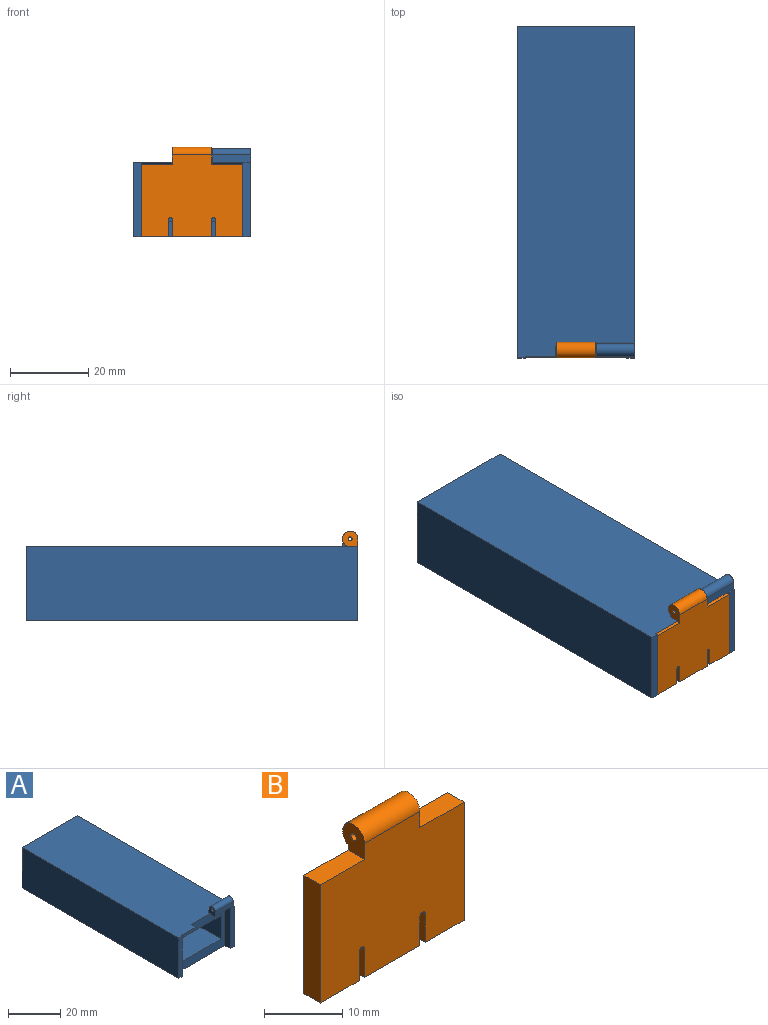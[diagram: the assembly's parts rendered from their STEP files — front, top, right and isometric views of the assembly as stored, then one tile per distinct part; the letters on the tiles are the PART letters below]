
ASSEMBLY  parts=2 mates=1
PART A: 26 faces, bbox 30x85x22.6 mm
  f0: plane 2x0.4mm, normal (0,0,1), area 0.8mm2, adj f6,f10,f12,f25
  f1: plane 19x2mm, normal (0,-1,0), area 38mm2, adj f3,f7,f9,f13
  f2: plane 7.8x1.8mm, normal (0,0,-1), area 14mm2, adj f4,f11,f13,f21
  f3: plane 85x30mm, normal (0,0,1), area 2476.5mm2, adj f1,f4,f5,f8,f9,f10,f11,f13
  f4: plane 2.6x0.5mm, normal (1,0,0), area 1.1mm2, adj f2,f3,f11,f21
  f5: plane 4.1x3.6mm, normal (-1,0,0), area 11.2mm2, adj f3,f11,f14,f20,f22,f23,f24,f25
  f6: plane 19x2mm, normal (0,-1,0), area 38mm2, adj f0,f7,f10,f12
  f7: plane 85x30mm, normal (0,0,-1), area 2472mm2, adj f1,f6,f8,f9,f10,f11,f12,f13
  f8: plane 30x19mm, normal (0,1,0), area 570mm2, adj f3,f7,f9,f10
  f9: plane 85x19mm, normal (-1,0,0), area 1615mm2, adj f1,f3,f7,f8
  f10: plane 85x22.6mm, normal (1,0,0), area 1625.1mm2, adj f0,f3,f6,f7,f8,f22,f23,f24
  f11: plane 26x19mm, normal (0,-1,0), area 244.2mm2, adj f2,f3,f4,f5,f7,f12,f13,f14
  f12: plane 19x3mm, normal (-1,0,0), area 55.9mm2, adj f0,f6,f7,f11,f14,f20
  f13: plane 19x3mm, normal (1,0,0), area 55.9mm2, adj f1,f2,f3,f7,f11,f21
  f14: plane 7.8x1.8mm, normal (0,0,-1), area 14mm2, adj f5,f11,f12,f20
  f15: plane 22x11mm, normal (0,-1,0), area 242mm2, adj f16,f17,f18,f19
  f16: plane 78x11mm, normal (1,0,0), area 858mm2, adj f11,f15,f17,f19
  f17: plane 78x22mm, normal (0,0,-1), area 1716mm2, adj f11,f15,f16,f18
  f18: plane 78x11mm, normal (-1,0,0), area 858mm2, adj f11,f15,f17,f19
  f19: plane 78x22mm, normal (0,0,1), area 1716mm2, adj f11,f15,f16,f18
  f20: cylinder r=2.69mm len=7.8mm, axis (1,0,0), area 7.4mm2, adj f5,f12,f14,f25
  f21: cylinder r=2.69mm len=7.8mm, axis (1,0,0), area 7.4mm2, adj f2,f3,f4,f13
  f22: cylinder r=1.6mm len=9.8mm, axis (-1,0,0), area 46.5mm2, adj f5,f10,f23,f25
  f23: plane 9.8x2.29mm, normal (0,0.98,0.18), area 22.8mm2, adj f3,f5,f10,f22
  f24: cylinder r=0.5mm len=9.8mm, axis (-1,0,0), area 30.8mm2, adj f5,f10
  f25: plane 9.8x2mm, normal (0,-1,0), area 19.6mm2, adj f0,f5,f10,f20,f22
PART B: 28 faces, bbox 26x11x23 mm
  f0: plane 11x10mm, normal (0,0,-1), area 110mm2, adj f4,f12,f18,f19
  f1: plane 7x3mm, normal (0,0,-1), area 21mm2, adj f2,f4,f7,f20
  f2: plane 26x19.27mm, normal (0,1,0), area 428.8mm2, adj f1,f3,f5,f6,f7,f8,f9,f10
  f3: cylinder r=2mm len=10mm, axis (-1,0,0), area 83.8mm2, adj f2,f4,f8,f10
  f4: plane 26x21mm, normal (0,-1,0), area 496.2mm2, adj f0,f1,f3,f5,f6,f7,f8,f9
  f5: plane 7x3mm, normal (0,0,-1), area 21mm2, adj f2,f4,f6,f21
  f6: plane 18.5x3mm, normal (1,0,0), area 55.5mm2, adj f2,f4,f5,f11
  f7: plane 18.5x3mm, normal (-1,0,0), area 55.5mm2, adj f1,f2,f4,f9
  f8: plane 4.5x4mm, normal (-1,0,0), area 14.2mm2, adj f2,f3,f4,f9,f27
  f9: plane 8x3mm, normal (0,0,1), area 24mm2, adj f2,f4,f7,f8
  f10: plane 4.5x4mm, normal (1,0,0), area 14.2mm2, adj f2,f3,f4,f11,f27
  f11: plane 8x3mm, normal (0,0,1), area 24mm2, adj f2,f4,f6,f10
  f12: plane 10x1.47mm, normal (0,1,0), area 14.7mm2, adj f0,f13,f18,f19
  f13: plane 10x3mm, normal (0,0.17,0.98), area 30.5mm2, adj f12,f14,f18,f19
  f14: plane 10x1mm, normal (0,1,0), area 10mm2, adj f13,f15,f18,f19
  f15: plane 10x1mm, normal (0,0,1), area 10mm2, adj f14,f16,f18,f19
  f16: plane 10x1mm, normal (0,-0.98,0.17), area 10.2mm2, adj f15,f17,f18,f19
  f17: plane 10x4.06mm, normal (0,0,1), area 40.6mm2, adj f16,f18,f19,f26
  f18: plane 11x4.5mm, normal (1,0,0), area 27.1mm2, adj f0,f4,f12,f13,f14,f15,f16,f17
  f19: plane 11x4.5mm, normal (-1,0,0), area 27.1mm2, adj f0,f4,f12,f13,f14,f15,f16,f17
  f20: plane 4.5x3mm, normal (1,0,0), area 13.5mm2, adj f1,f2,f4,f22
  f21: plane 4.5x3mm, normal (-1,0,0), area 13.5mm2, adj f2,f4,f5,f23
  f22: cylinder r=0.5mm len=3mm, axis (0,1,0), area 4.3mm2, adj f2,f4,f19,f20,f25
  f23: cylinder r=0.5mm len=3mm, axis (0,-1,0), area 4.3mm2, adj f2,f4,f18,f21,f25
  f24: plane 10x1mm, normal (0,0.97,-0.23), area 10.3mm2, adj f18,f19,f25,f26
  f25: cylinder r=1mm len=11mm, axis (1,0,0), area 13.8mm2, adj f2,f18,f19,f22,f23,f24
  f26: cylinder r=1mm len=10mm, axis (-1,0,0), area 18mm2, adj f17,f18,f19,f24
  f27: cylinder r=0.5mm len=10mm, axis (1,0,0), area 31.4mm2, adj f8,f10
PLACE A at identity fixed
PLACE B rot(axis=(-1,0,0),0deg) t=(0,0,0)mm
MATE revolute B.f3 <-> A.f22  axis (-1,0,0) through (0,-38.5,11.5)mm
